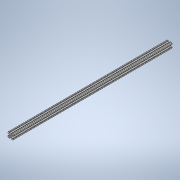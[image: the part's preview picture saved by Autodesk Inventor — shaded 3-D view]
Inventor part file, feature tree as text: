
AUTODESK INVENTOR PART (.ipt)
format: ipt  version: 2020 (Build 240168000, 168)  size: 241,152 bytes
history: native  units: in
note: dims shown in document units (in); Inventor stores cm internally (conversion verified against a paired STEP export)
features: extrude x1, sketch x1
ambient origin geometry x8: Origin, YZ Plane, XZ Plane, XY Plane, X Axis, Y Axis, Z Axis, Center Point
bodies: Solid1 (feature_tree)
feature tree (2):
  extrude  "Extrusion1"  [1 undecoded]
  sketch  "Sketch1"  dims[d0=30.0in d1=0.0in]
note: 1 required parameter value undecoded (feature->parameter linkage not recoverable at this tier; creation-order binding heuristic only, values carry confidence <= 0.55)
